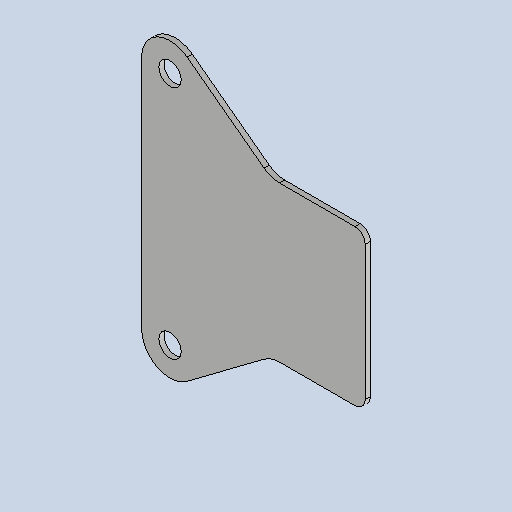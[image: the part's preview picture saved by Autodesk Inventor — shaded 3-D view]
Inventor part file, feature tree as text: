
AUTODESK INVENTOR PART (.ipt)
format: ipt  version: 2025 (Build 290162010, 162A)  size: 128,512 bytes
history: native  units: mm
features: sheet_metal_op x1, chamfer x1, mirror x1, sketch x1, other x1
ambient origin geometry x8: Origin, YZ Plane, XZ Plane, XY Plane, X Axis, Y Axis, Z Axis, Center Point
bodies: Solid1 (feature_tree)
feature tree (5):
  sheet_metal_op  "Face1"
  chamfer  "Corner Round2"
  mirror  "Mirror1"
  sketch  "Sketch1"  dims[d2=80.0mm d3=80.0mm d6=3.0mm d25=6.0mm d29=5.0mm d30=13.0mm d31=10.0mm d32=40.0mm d33=6.429331mm d34=5.0mm d35=15.0mm]
  other  "Plate1"
